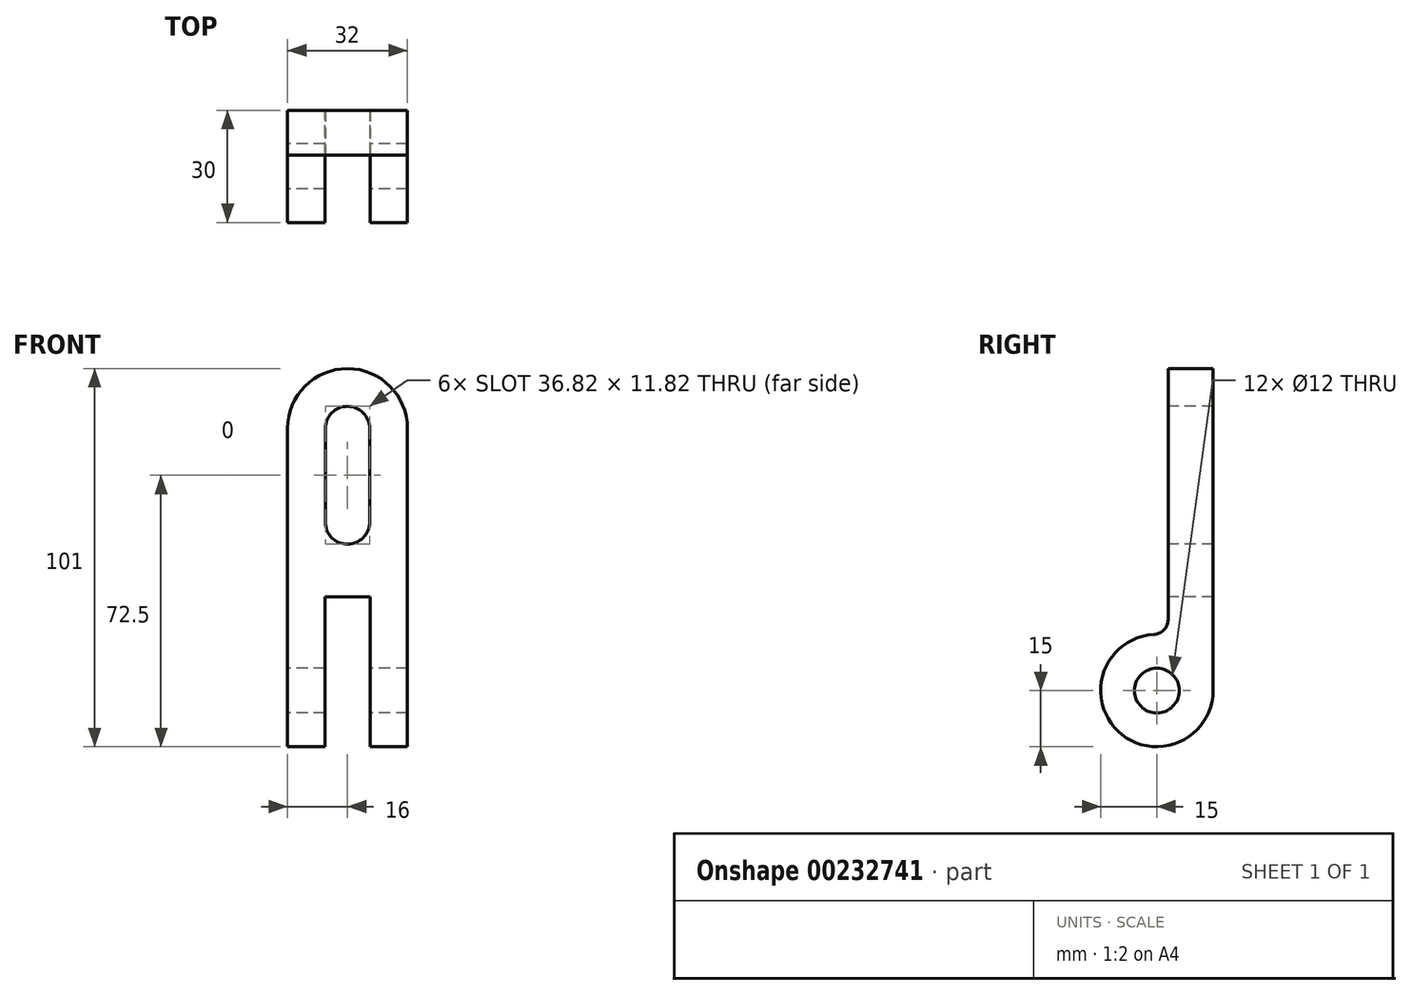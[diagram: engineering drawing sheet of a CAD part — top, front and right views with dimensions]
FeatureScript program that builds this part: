
annotation { "Feature Type Name" : "Feature", "Feature Type Description" : "" }
export const myFeature = defineFeature(function(context is Context, id is Id, definition is map)
    precondition{}
    {
        {
            var Q0;
            Q0=qCreatedBy(makeId("Right.planeOp"),FACE);
            var sketch = newSketch(context, id + "F0", { "sketchPlane" : qUnion([Q0])});
            skLineSegment(sketch, "E0", {"start": v(0, 0) * mm, "end": v(12, 0) * mm});
            skLineSegment(sketch, "E1", {"start": v(12, 0) * mm, "end": v(12, -86) * mm});
            skLineSegment(sketch, "E2", {"start": v(0, 0) * mm, "end": v(0, -67.03) * mm});
            skCircle(sketch, "E3", {"center": v(-3, -86) * mm, "radius": 6 * mm});
            skArc(sketch, "E4", {"start": v(-3.79, -71.02) * mm, "mid": v(-13.32, -96.88) * mm, "end": v(12, -86) * mm});
            skPoint(sketch, "E5.visualSharp", {"position": v(0, -71.3) * mm});
            skArc(sketch, "E5.filletArc", {"start": v(-3.79, -71.02) * mm, "mid": v(-1.1, -69.78) * mm, "end": v(0, -67.03) * mm});
            skSolve(sketch);
        }
        {
            var Q0;
            Q0=makeQuery(id+"F0.imprint","IMPRINT",FACE,{"disambiguationData":[TD([[makeQuery(id+"F0.imprint","IMPRINT",EDGE,{"derivedFrom":sQuery(id+"F0.wireOp",EDGE,"E0")}),-1.0]])]});
            extrude(context, id + "F1", {"entities" : qUnion([Q0]), "depth" : 32 * mm});
        }
        {
            var Q0;
            Q0=makeQuery(id+"F1.opExtrude","SWEPT_FACE",FACE,{"disambiguationData":[OSD([sQuery(id+"F0.wireOp",EDGE,"E2")])]});
            var sketch = newSketch(context, id + "F2", { "sketchPlane" : qUnion([Q0])});
            skLineSegment(sketch, "E6.0.0", {"start": v(0, 0) * mm, "end": v(0, -67.03) * mm, "construction": true});
            skLineSegment(sketch, "E6.0.1", {"start": v(0, -67.03) * mm, "end": v(32, -67.03) * mm, "construction": true});
            skLineSegment(sketch, "E6.0.2", {"start": v(32, -67.03) * mm, "end": v(32, 0) * mm, "construction": true});
            skLineSegment(sketch, "E6.0.3", {"start": v(32, 0) * mm, "end": v(0, 0) * mm, "construction": true});
            skLineSegment(sketch, "E7", {"start": v(32, -101) * mm, "end": v(0, -101) * mm, "construction": true});
            skLineSegment(sketch, "E8.0.0", {"start": v(0, -67.03) * mm, "end": v(0, -71.02) * mm, "construction": true});
            skLineSegment(sketch, "E8.0.1", {"start": v(0, -71.02) * mm, "end": v(32, -71.02) * mm, "construction": true});
            skLineSegment(sketch, "E8.0.2", {"start": v(32, -71.02) * mm, "end": v(32, -67.03) * mm, "construction": true});
            skLineSegment(sketch, "E8.0.3", {"start": v(32, -67.03) * mm, "end": v(0, -67.03) * mm, "construction": true});
            skLineSegment(sketch, "E9.bottom", {"start": v(21.91, -41) * mm, "end": v(10.09, -41) * mm});
            skLineSegment(sketch, "E9.top", {"start": v(21.91, -16) * mm, "end": v(10.09, -16) * mm});
            skLineSegment(sketch, "E9.left", {"start": v(21.91, -41) * mm, "end": v(21.91, -16) * mm});
            skLineSegment(sketch, "E9.right", {"start": v(10.09, -41) * mm, "end": v(10.09, -16) * mm});
            skLineSegment(sketch, "E10.bottom", {"start": v(22, -101) * mm, "end": v(10, -101) * mm});
            skLineSegment(sketch, "E10.top", {"start": v(22, -61) * mm, "end": v(10, -61) * mm});
            skLineSegment(sketch, "E10.left", {"start": v(22, -101) * mm, "end": v(22, -61) * mm});
            skLineSegment(sketch, "E10.right", {"start": v(10, -101) * mm, "end": v(10, -61) * mm});
            skArc(sketch, "E11", {"start": v(21.91, -41) * mm, "mid": v(16, -46.91) * mm, "end": v(10.09, -41) * mm});
            skArc(sketch, "E12", {"start": v(21.91, -16) * mm, "mid": v(16, -10.09) * mm, "end": v(10.09, -16) * mm});
            skArc(sketch, "E13", {"start": v(32, -16) * mm, "mid": v(16, 0) * mm, "end": v(0, -16) * mm});
            skPoint(sketch, "E14", {"position": v(16, -101) * mm});
            skSolve(sketch);
        }
        {
            var Q0;
            {var subQ0=sQuery(id+"F2.wireOp",EDGE,"E10.top");Q0=makeQuery(id+"F2.imprint","IMPRINT",FACE,{"disambiguationData":[TD([[makeQuery(id+"F2.imprint","IMPRINT",EDGE,{"derivedFrom":subQ0}),1.0]])]});}
            var Q1;
            Q1=makeQuery(id+"F2.imprint","IMPRINT",FACE,{"disambiguationData":[TD([[makeQuery(id+"F2.imprint","IMPRINT",EDGE,{"derivedFrom":sQuery(id+"F2.wireOp",EDGE,"E9.bottom")}),1.0]])]});
            var Q2;
            Q2=makeQuery(id+"F2.imprint","IMPRINT",FACE,{"disambiguationData":[TD([[makeQuery(id+"F2.imprint","IMPRINT",EDGE,{"derivedFrom":sQuery(id+"F2.wireOp",EDGE,"E9.bottom")}),-1.0]])]});
            var Q3;
            Q3=makeQuery(id+"F2.imprint","IMPRINT",FACE,{"disambiguationData":[TD([[makeQuery(id+"F2.imprint","IMPRINT",EDGE,{"derivedFrom":sQuery(id+"F2.wireOp",EDGE,"E9.top")}),-1.0]])]});
            var Q4;
            {var subQ0=sQuery(id+"F2.wireOp",EDGE,"E13");var subQ1=sQuery(id+"F0.wireOp",EDGE,"E2");var subQ2=makeQuery(id+"F1.opExtrude","CAP_EDGE",EDGE,{"disambiguationData":[OSD([subQ1])],"isStart":false});var subQ3=makeQuery(id+"F2.imprint","INTERSECT",VERTEX,{"derivedFrom":[subQ2,subQ0]});Q4=makeQuery(id+"F2.imprint","IMPRINT",FACE,{"disambiguationData":[TD([[makeQuery(id+"F2.imprint","IMPRINT",EDGE,{"disambiguationData":[TD([[subQ3,-1.0]])],"derivedFrom":subQ0}),-1.0]])]});}
            var Q5;
            {var subQ0=sQuery(id+"F2.wireOp",EDGE,"E13");var subQ1=sQuery(id+"F0.wireOp",EDGE,"E2");var subQ2=makeQuery(id+"F1.opExtrude","CAP_EDGE",EDGE,{"disambiguationData":[OSD([subQ1])],"isStart":true});var subQ3=makeQuery(id+"F2.imprint","INTERSECT",VERTEX,{"derivedFrom":[subQ2,subQ0]});Q5=makeQuery(id+"F2.imprint","IMPRINT",FACE,{"disambiguationData":[TD([[makeQuery(id+"F2.imprint","IMPRINT",EDGE,{"disambiguationData":[TD([[subQ3,1.0]])],"derivedFrom":subQ0}),-1.0]])]});}
            var Q6;
            {var subQ0=sQuery(id+"F2.wireOp",EDGE,"E10.bottom");Q6=makeQuery(id+"F2.imprint","IMPRINT",FACE,{"disambiguationData":[TD([[makeQuery(id+"F2.imprint","IMPRINT",EDGE,{"derivedFrom":subQ0}),-1.0]])]});}
            extrude(context, id + "F3", {"entities" : qUnion([Q0, Q1, Q2, Q3, Q4, Q5, Q6]), "operationType" : NewBodyOperationType.REMOVE, "endBound" : BoundingType.SYMMETRIC, "oppositeDirection" : true, "depth" : 40 * mm});
        }
    });
